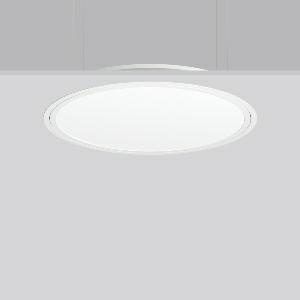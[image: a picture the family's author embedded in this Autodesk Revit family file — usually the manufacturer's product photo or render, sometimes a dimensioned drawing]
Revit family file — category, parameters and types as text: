
# Revit family: triona_round_e_312383_002_12_7031
name_source: partatom
category: Lighting Fixtures
units: mm (PartAtom-declared; Revit-internal decimal feet)

## family parameters
Cut with Voids When Loaded = No
Host = Face
Light Source = No
Part Type = Normal
Room Calculation Point = No
Round Connector Dimension = Use Diameter
Shared = No

## types (1)
- TRIONA round E (1 x LED Modul 830, 6450 lm, 3000)
    Apparent Load = 70 VA
    CIE Flux Codes = 49 80 96 100 100
    Color Rendering = 80
    Color Temperature = 3000
    Default Elevation = 1800 mm
    Description = Series: TRIONA round
Decorative round LED recessed surface luminaire. Cover made of sheet steel, powder-coated. Frame made of aluminium, powder-coated. Recessed ring: aluminium extrusion profile, powder coated. Light emission through a diffuser: plastic, opal. Lightguide and diffuser made of non-yellowing plastic (PMMA). Lateral light emission (RZB SIDELITE technology) for above-average homogeneous light distribution. Suitable for installation in cavity ceilings. Tool-free mounting system thanks to the rocker arm mechanism (patent pending). Electronic ballast included. Very easy installation thanks to Plug+Play connection. 
Colour: traffic white, matt (RAL 9016)
Diameter: 725 mm
Height: 2 mm
Cut-out diameter: 702 mm
Recess height: 100 mm
Luminaire: recess height: 89 mm
Lamp: LED
Socket: without socket
Colour temperature: 3000K
Colour rendering index (CRI): 80
System power: 70 W
Rated luminous flux: 6450 lm
Luminous efficiency: 92 lm/W
Control gear: Converter, dimmable, DALI
Protection class: I
Type of protection: IP 40
    Height = 0 mm  [stored 0 ft]
    Lamp = 1 x LED Modul 830
    Lamp Light Flux = 6450 lm
    Lamp count = 1
    Length = 725 mm
    Lifetime = 50000 h
    Luminous efficacy = 92 lm/W
    Manufacturer = RZB
    ModVariant = No
    Model = 312383.002.12
    Mounting Place = Ceiling
    Mounting Type = Recessed
    Number of Poles = 1
    OnlyDefault = Yes
    Power Factor = 1
    Product Name = TRIONA round E
    Product group = Recessed modular luminaires
    ProductGroupID = 406
    Protection Class = Protection class I
    Protection Degree = IP 20
    RLX_Detail_Level = 1
    RLX_Emergency_Light_Flux = 0 lm
    RLX_Emergency_Type = 0
    RLX_Emergency_Type_DB = No
    RlxData = <blob elided: 34833 chars, md5=bc99bd97>
    Socket = socket
    Standby Power = 0 W
    System Light Flux = 6450 lm
    System Power = 70 W
    Type Comments = Product without accessories
    Type Image = 312383.002.12.jpg
    URL = http://relux.com
    VarID = ---
    Voltage = 230 V
    Voltage Range = 220-240 V
    Weight = 0.00 kg
    Width = 0 mm  [stored 0 ft]

note: [stored X ft] marks values corroborated as IEEE doubles in the binary element streams (Revit-internal decimal feet)

## geometry (parser evidence)
native form markers: Blend x4, Sweep x9
no freeform markers — native parametric forms only
